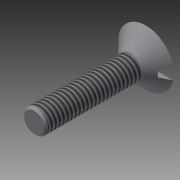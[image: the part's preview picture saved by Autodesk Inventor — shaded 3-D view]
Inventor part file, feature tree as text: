
AUTODESK INVENTOR PART (.ipt)
format: ipt  version: 2015 (Build 190159000, 159)  size: 112,128 bytes
history: native  units: mm
features: sketch x3, extrude x2, revolve x1, chamfer x1, thread x1, plane x1
ambient origin geometry x8: Origin, YZ Plane, XZ Plane, XY Plane, X Axis, Y Axis, Z Axis, Center Point
bodies: 实体1 (feature_tree)
feature tree (9):
  revolve  "旋转1"  [1 undecoded]
  extrude  "拉伸1"  TaperAngle=90.0deg  [1 undecoded]
  chamfer  "倒角1"  Distance=12.0mm
  thread  "螺纹1"  [1 undecoded]
  plane  "工作平面1"
  extrude  "拉伸2"  Depth=1.0mm TaperAngle=0.0deg
  sketch  "草图1"  dims[d0=3.5mm d1=2.0mm]
  sketch  "草图2"  dims[d2=1.5mm d3=90.0deg]
  sketch  "草图3"  dims[d4=3.0mm d5=12.0mm d6=0.0mm d7=0.25mm d8=2.0mm d9=45.0deg d10=10.0mm d11=0.0mm d12=3.5mm d13=1.0mm d14=0.8mm d15=1.5mm d16=7.0mm d17=0.0mm]
note: 3 required parameter values undecoded (feature->parameter linkage not recoverable at this tier; creation-order binding heuristic only, values carry confidence <= 0.55)